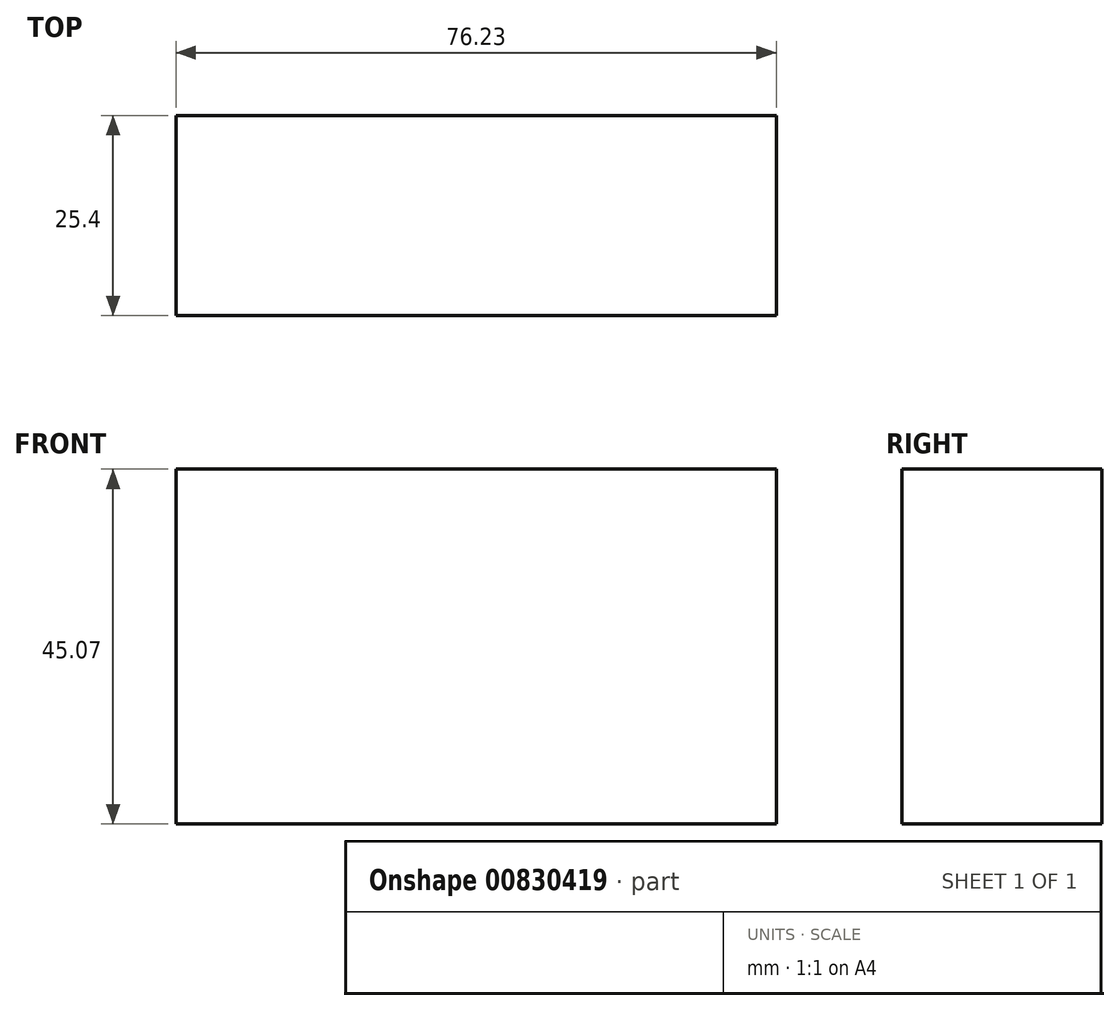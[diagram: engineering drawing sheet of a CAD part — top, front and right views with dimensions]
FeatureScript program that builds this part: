
annotation { "Feature Type Name" : "Feature", "Feature Type Description" : "" }
export const myFeature = defineFeature(function(context is Context, id is Id, definition is map)
    precondition{}
    {
        {
            var Q0;
            Q0=qCreatedBy(makeId("Front.planeOp"),FACE);
            var sketch = newSketch(context, id + "F0", { "sketchPlane" : qUnion([Q0])});
            skLineSegment(sketch, "E0.bottom", {"start": v(0, 45.07) * mm, "end": v(76.23, 45.07) * mm});
            skLineSegment(sketch, "E0.top", {"start": v(0, 0) * mm, "end": v(76.23, 0) * mm});
            skLineSegment(sketch, "E0.left", {"start": v(0, 45.07) * mm, "end": v(0, 0) * mm});
            skLineSegment(sketch, "E0.right", {"start": v(76.23, 45.07) * mm, "end": v(76.23, 0) * mm});
            skSolve(sketch);
        }
        {
            var Q0;
            Q0=makeQuery(id+"F0.imprint","IMPRINT",FACE,{"disambiguationData":[TD([[makeQuery(id+"F0.imprint","IMPRINT",EDGE,{"derivedFrom":sQuery(id+"F0.wireOp",EDGE,"E0.bottom")}),-1.0]])]});
            extrude(context, id + "F1", {"entities" : qUnion([Q0]), "depth" : 25.4 * mm, "offsetDistance" : 25.4 * mm});
        }
    });
